# Revit family: SONNIGER - Nagrzewnica wodna HEATER CONDENS - CR ONE, CR1, CR2, CR3, CR3 MAX, CR4 MAX
name_source: partatom
category: Wyposażenie mechaniczne
revit_build: Autodesk Revit 2018 (Build: 20170927_1515(x64)
units: mm (PartAtom-declared; Revit-internal decimal feet)

## family parameters
Klasyfikacja = Brak
Obiekt nadrzędny = Powierzchnia
Punkt obliczania pomieszczeń = Nie
Tnij formami wycięć po wczytaniu = Nie
Typ części = Normalny
Współdzielony = Nie
Wymiar okrągłego złącza = Użyj średnicy

## types (14) — shared parameters
Autor = www.archispace.com
Domyślna rzędna = 1219.200 mm
O = 130.000 mm
Opis = Nagrzewnica wodna
Producent = SONNIGER Polska Sp. z o.o. Sp. k.
klasa IP = IP54
maksymalna temp. czynnika = 120 °C
maksymalne ciśnienie robocze = 1600000.0 Pa
materiał = 230,230,230
napięcie zasilania = 230 V
zero-valued in all types: głośność pracy (dB)

## per-type parameters (varying)
| type | H | Model | O1 | S g | W g | ilość rzędów nagrzewnicy | maksymalny wydatek powietrza | maksymalny zasięg powietrza | moc grzewcza max. | moc grzewcza min. | moc silnika elektrycznego | obroty silnika (obr/min) | poziom głośności pracy | waga bez wody | waga z wodą | ΔT |
| CR ONE - montaż naścienny | 18536.143 mm | Heater CONDENS CR ONE | Tak | 13120.000 mm | 13850.000 mm | 2 | 1600.0 m³/h | 14000.000 mm | 25 kW | 5 kW | 124 W | 1400 | I bieg 35 dB / II bieg 46 dB / III bieg 52 dB | 9.60 kg | 10.70 kg | 25 °C |
| CR1 - montaż naścienny | 26136.143 mm | Heater CONDENS CR1 | Tak | 16000.000 mm | 16000.000 mm | 1 | 3900.0 m³/h | 24000.000 mm | 35 kW | 10 kW | 250 W | 1350 | I bieg 44 dB / II bieg 52 dB / III bieg 62 dB | 10.80 kg | 11.90 kg | 13 °C |
| CR2 - montaż naścienny | 24536.143 mm | Heater CONDENS CR2 | Tak | 15900.000 mm | 15100.000 mm | 2 | 3350.0 m³/h | 21000.000 mm | 50 kW | 15 kW | 250 W | 1350 | I bieg 41 dB / II bieg 50 dB / III bieg 60 dB | 12.70 kg | 14.80 kg | 22 °C |
| CR3 - montaż naścienny | 22936.143 mm | Heater CONDENS CR3 | Tak | 15400.000 mm | 14600.000 mm | 3 | 2950.0 m³/h | 19000.000 mm | 70 kW | 20 kW | 250 W | 1350 | I bieg 39 dB / II bieg 48 dB / III bieg 58 dB | 14.50 kg | 16.90 kg | 34 °C |
| CR ONE - montaż na suficie | 9536.143 mm | Heater CONDENS CR ONE | Tak | 9100.000 mm | 9900.000 mm | 2 | 1600.0 m³/h | 14000.000 mm | 25 kW | 5 kW | 124 W | 1400 | I bieg 35 dB / II bieg 46 dB / III bieg 52 dB | 9.60 kg | 10.70 kg | 25 °C |
| CR1 - montaż na suficie | 12536.143 mm | Heater CONDENS CR1 | Tak | 11420.000 mm | 10510.000 mm | 1 | 3900.0 m³/h | 24000.000 mm | 35 kW | 10 kW | 250 W | 1350 | I bieg 44 dB / II bieg 52 dB / III bieg 62 dB | 10.80 kg | 11.90 kg | 13 °C |
| CR2 - montaż na suficie | 11836.143 mm | Heater CONDENS CR2 | Tak | 10900.000 mm | 10360.000 mm | 2 | 3350.0 m³/h | 21000.000 mm | 50 kW | 15 kW | 250 W | 1350 | I bieg 41 dB / II bieg 50 dB / III bieg 60 dB | 12.70 kg | 14.80 kg | 22 °C |
| CR3 - montaż na suficie | 11036.143 mm | Heater CONDENS CR3 | Tak | 10760.000 mm | 9760.000 mm | 3 | 2950.0 m³/h | 19000.000 mm | 70 kW | 20 kW | 250 W | 1350 | I bieg 39 dB / II bieg 48 dB / III bieg 58 dB | 14.50 kg | 16.90 kg | 34 °C |
| CR2 MAX - montaż na suficie | 14860.341 mm | Heater CONDENS CR2 MAX | Nie | 12470.000 mm | 11470.000 mm | 2 | 5700.0 m³/h | 26000.000 mm | 70 kW | 25 kW | 520 W | 1380 | I bieg 41 dB / II bieg 50 dB / III bieg 59 dB | 23.60 kg | 25.20 kg | 22 °C |
| CR2 MAX - montaż naścienny | 13536.341 mm | Heater CONDENS CR2 MAX | Nie | 19500.000 mm | 19500.000 mm | 2 | 5700.0 m³/h | 26000.000 mm | 70 kW | 25 kW | 520 W | 1380 | I bieg 41 dB / II bieg 50 dB / III bieg 59 dB | 23.60 kg | 25.20 kg | 22 °C |
| CR3 MAX - montaż na suficie | 14060.341 mm | Heater CONDENS CR3 MAX | Nie | 12000.000 mm | 11250.000 mm | 3 | 5600.0 m³/h | 25000.000 mm | 95 kW | 35 kW | 520 W | 1380 | I bieg 40 dB / II bieg 48 dB / III bieg 58 dB | 25.20 kg | 27.40 kg | 35 °C |
| CR3 MAX - montaż naścienny | 31160.341 mm | Heater CONDENS CR3 MAX | Nie | 17900.000 mm | 17100.000 mm | 3 | 5600.0 m³/h | 25000.000 mm | 95 kW | 35 kW | 520 W | 1380 | I bieg 40 dB / II bieg 48 dB / III bieg 58 dB | 25.50 kg | 27.40 kg | 35 °C |
| CR4 MAX - montaż na suficie | 13360.341 mm | Heater CONDENS CR4 MAX | Nie | 11820.000 mm | 10830.000 mm | 3 | 5100.0 m³/h | 23000.000 mm | 120 kW | 40 kW | 520 W | 1380 | I bieg 40 dB / II bieg 48 dB / III bieg 58 dB | 25.50 kg | 28.00 kg | 44 °C |
| CR4 MAX - montaż naścienny | 32860.341 mm | Heater CONDENS CR4 MAX | Nie | 18400.000 mm | 17550.000 mm | 3 | 5100.0 m³/h | 23000.000 mm | 120 kW | 40 kW | 520 W | 1380 | I bieg 40 dB / II bieg 48 dB / III bieg 58 dB | 25.50 kg | 28.00 kg | 44 °C |
